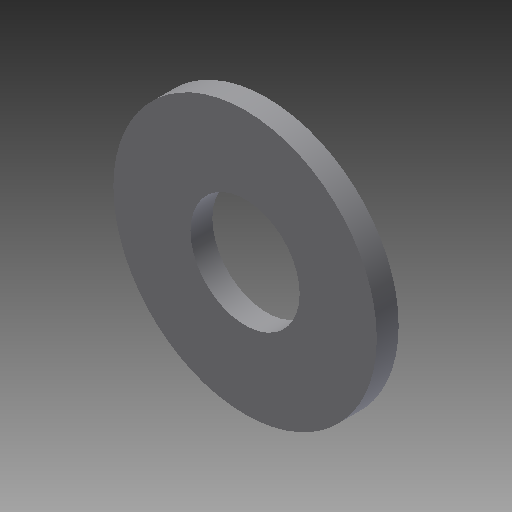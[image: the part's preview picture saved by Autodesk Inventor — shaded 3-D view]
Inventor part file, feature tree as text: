
AUTODESK INVENTOR PART (.ipt)
format: ipt  version: 2019 (Build 230136000, 136)  size: 99,840 bytes
history: native  units: in
note: dims shown in document units (in); Inventor stores cm internally (conversion verified against a paired STEP export)
features: other x7, extrude x1, sketch x1
ambient origin geometry x8: Origin, YZ Plane, XZ Plane, XY Plane, X Axis, Y Axis, Z Axis, Center Point
bodies: Solid1 (feature_tree)
feature tree (9):
  extrude  "Extrusion1"  TaperAngle=0.0deg  [1 undecoded]
  other  "to_a_XY"
  other  "to_a_YZ"
  other  "to_a_ZX"
  other  "to_a_X"
  other  "to_a_Y"
  other  "to_a_Z"
  other  "to_a_Center"
  sketch  "Sketch_1"  dims[d0=0.065in d1=0.0in d2=0.0in]
note: 1 required parameter value undecoded (feature->parameter linkage not recoverable at this tier; creation-order binding heuristic only, values carry confidence <= 0.55)
